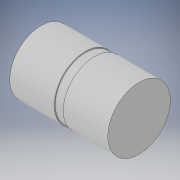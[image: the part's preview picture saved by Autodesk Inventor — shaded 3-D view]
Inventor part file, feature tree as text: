
AUTODESK INVENTOR PART (.ipt)
format: ipt  version: 2019 (Build 230136000, 136)  size: 219,136 bytes
history: native  units: mm
features: revolve x1, sketch x1
ambient origin geometry x8: Origin, YZ Plane, XZ Plane, XY Plane, X Axis, Y Axis, Z Axis, Center Point
bodies: Solid1 (feature_tree)
feature tree (2):
  revolve  "Revolution1"  [1 undecoded]
  sketch  "Sketch1"  dims[d1=1.0mm d2=10.0mm d3=50.0mm d4=50.0mm d5=1.0mm d8=2.5mm d9=35.0mm d10=30.0mm d12=30.0mm d13=90.0deg d14=110.0mm]
note: 1 required parameter value undecoded (feature->parameter linkage not recoverable at this tier; creation-order binding heuristic only, values carry confidence <= 0.55)
